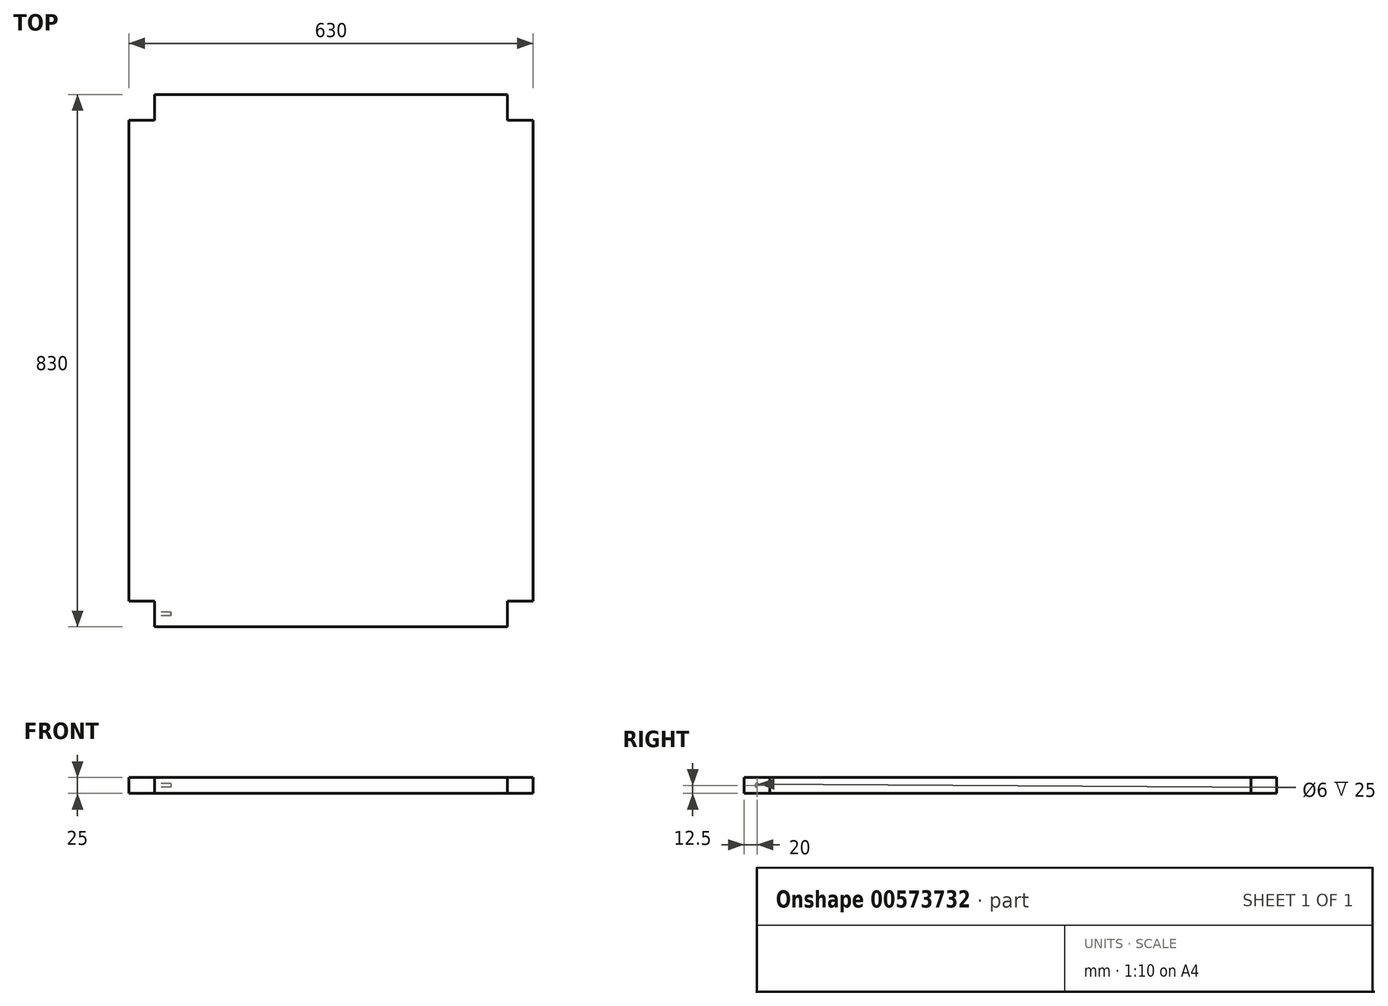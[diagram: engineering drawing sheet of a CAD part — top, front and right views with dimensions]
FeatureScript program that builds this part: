
annotation { "Feature Type Name" : "Feature", "Feature Type Description" : "" }
export const myFeature = defineFeature(function(context is Context, id is Id, definition is map)
    precondition{}
    {
        {
            var Q0;
            Q0=qCreatedBy(makeId("Top.planeOp"),FACE);
            var sketch = newSketch(context, id + "F0", { "sketchPlane" : qUnion([Q0])});
            skLineSegment(sketch, "E0.bottom", {"start": v(0, 0) * mm, "end": v(630, 0) * mm});
            skLineSegment(sketch, "E0.top", {"start": v(0, 830) * mm, "end": v(630, 830) * mm});
            skLineSegment(sketch, "E0.left", {"start": v(0, 0) * mm, "end": v(0, 830) * mm});
            skLineSegment(sketch, "E0.right", {"start": v(630, 0) * mm, "end": v(630, 830) * mm});
            skSolve(sketch);
        }
        {
            var Q0;
            Q0=makeQuery(id+"F0.imprint","IMPRINT",FACE,{"disambiguationData":[TD([[makeQuery(id+"F0.imprint","IMPRINT",EDGE,{"derivedFrom":sQuery(id+"F0.wireOp",EDGE,"E0.bottom")}),1.0]])]});
            extrude(context, id + "F1", {"entities" : qUnion([Q0]), "depth" : 25 * mm, "offsetDistance" : 25 * mm});
        }
        {
            var Q0;
            Q0=makeQuery(id+"F1.opExtrude","CAP_FACE",FACE,{"disambiguationData":[OSD([sQuery(id+"F0.wireOp",EDGE,"E0.bottom"),sQuery(id+"F0.wireOp",EDGE,"E0.top"),sQuery(id+"F0.wireOp",EDGE,"E0.left"),sQuery(id+"F0.wireOp",EDGE,"E0.right")])],"isStart":false});
            var sketch = newSketch(context, id + "F2", { "sketchPlane" : qUnion([Q0])});
            skLineSegment(sketch, "E1.bottom", {"start": v(590, 0) * mm, "end": v(630, 0) * mm});
            skLineSegment(sketch, "E1.top", {"start": v(590, 40) * mm, "end": v(630, 40) * mm});
            skLineSegment(sketch, "E1.left", {"start": v(590, 0) * mm, "end": v(590, 40) * mm});
            skLineSegment(sketch, "E1.right", {"start": v(630, 0) * mm, "end": v(630, 40) * mm});
            skSolve(sketch);
        }
        {
            var Q0;
            Q0 = qSketchRegion(id + "F2", true);
            extrude(context, id + "F3", {"entities" : qUnion([Q0]), "operationType" : NewBodyOperationType.REMOVE, "oppositeDirection" : true, "depth" : 25 * mm, "offsetDistance" : 25 * mm});
        }
        {
            var Q0;
            Q0=makeQuery(id+"F1.opExtrude","CAP_FACE",FACE,{"disambiguationData":[OSD([sQuery(id+"F0.wireOp",EDGE,"E0.bottom"),sQuery(id+"F0.wireOp",EDGE,"E0.top"),sQuery(id+"F0.wireOp",EDGE,"E0.left"),sQuery(id+"F0.wireOp",EDGE,"E0.right")])],"isStart":false});
            var sketch = newSketch(context, id + "F4", { "sketchPlane" : qUnion([Q0])});
            skLineSegment(sketch, "E2.bottom", {"start": v(0, 0) * mm, "end": v(40, 0) * mm});
            skLineSegment(sketch, "E2.top", {"start": v(0, 40) * mm, "end": v(40, 40) * mm});
            skLineSegment(sketch, "E2.left", {"start": v(0, 0) * mm, "end": v(0, 40) * mm});
            skLineSegment(sketch, "E2.right", {"start": v(40, 0) * mm, "end": v(40, 40) * mm});
            skSolve(sketch);
        }
        {
            var Q0;
            Q0 = qSketchRegion(id + "F4", true);
            extrude(context, id + "F5", {"entities" : qUnion([Q0]), "operationType" : NewBodyOperationType.REMOVE, "oppositeDirection" : true, "depth" : 25 * mm, "offsetDistance" : 25 * mm});
        }
        {
            var Q0;
            Q0=makeQuery(id+"F1.opExtrude","CAP_FACE",FACE,{"disambiguationData":[OSD([sQuery(id+"F0.wireOp",EDGE,"E0.bottom"),sQuery(id+"F0.wireOp",EDGE,"E0.top"),sQuery(id+"F0.wireOp",EDGE,"E0.left"),sQuery(id+"F0.wireOp",EDGE,"E0.right")])],"isStart":true});
            var sketch = newSketch(context, id + "F6", { "sketchPlane" : qUnion([Q0])});
            skLineSegment(sketch, "E3.bottom", {"start": v(0, -830) * mm, "end": v(40, -830) * mm});
            skLineSegment(sketch, "E3.top", {"start": v(0, -790) * mm, "end": v(40, -790) * mm});
            skLineSegment(sketch, "E3.left", {"start": v(0, -830) * mm, "end": v(0, -790) * mm});
            skLineSegment(sketch, "E3.right", {"start": v(40, -830) * mm, "end": v(40, -790) * mm});
            skSolve(sketch);
        }
        {
            var Q0;
            Q0 = qSketchRegion(id + "F6", true);
            extrude(context, id + "F7", {"entities" : qUnion([Q0]), "operationType" : NewBodyOperationType.REMOVE, "oppositeDirection" : true, "depth" : 25 * mm, "offsetDistance" : 25 * mm});
        }
        {
            var Q0;
            Q0=makeQuery(id+"F1.opExtrude","CAP_FACE",FACE,{"disambiguationData":[OSD([sQuery(id+"F0.wireOp",EDGE,"E0.bottom"),sQuery(id+"F0.wireOp",EDGE,"E0.top"),sQuery(id+"F0.wireOp",EDGE,"E0.left"),sQuery(id+"F0.wireOp",EDGE,"E0.right")])],"isStart":true});
            var sketch = newSketch(context, id + "F8", { "sketchPlane" : qUnion([Q0])});
            skLineSegment(sketch, "E4.bottom", {"start": v(630, -830) * mm, "end": v(590, -830) * mm});
            skLineSegment(sketch, "E4.top", {"start": v(630, -790) * mm, "end": v(590, -790) * mm});
            skLineSegment(sketch, "E4.left", {"start": v(630, -830) * mm, "end": v(630, -790) * mm});
            skLineSegment(sketch, "E4.right", {"start": v(590, -830) * mm, "end": v(590, -790) * mm});
            skSolve(sketch);
        }
        {
            var Q0;
            Q0 = qSketchRegion(id + "F8", true);
            extrude(context, id + "F9", {"entities" : qUnion([Q0]), "operationType" : NewBodyOperationType.REMOVE, "oppositeDirection" : true, "depth" : 25 * mm, "offsetDistance" : 25 * mm});
        }
        {
            var Q0;
            Q0=makeQuery(id+"F5.boolean.opBoolean","COPY",FACE,{"derivedFrom":makeQuery(id+"F5.opExtrude","SWEPT_FACE",FACE,{"disambiguationData":[OSD([sQuery(id+"F4.wireOp",EDGE,"E2.right")])]})});
            var sketch = newSketch(context, id + "F10", { "sketchPlane" : qUnion([Q0])});
            skCircle(sketch, "E5", {"center": v(-20, 12.5) * mm, "radius": 3 * mm});
            skSolve(sketch);
        }
        {
            var Q0;
            Q0 = qSketchRegion(id + "F10", true);
            extrude(context, id + "F11", {"entities" : qUnion([Q0]), "operationType" : NewBodyOperationType.REMOVE, "oppositeDirection" : true, "depth" : 25 * mm, "offsetDistance" : 25 * mm});
        }
    });
